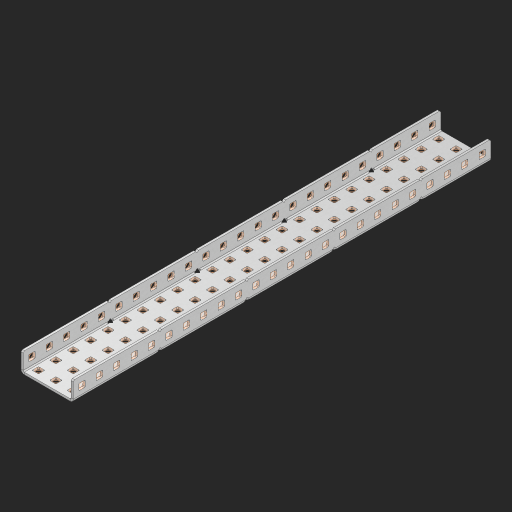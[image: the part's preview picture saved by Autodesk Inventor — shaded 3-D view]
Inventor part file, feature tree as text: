
AUTODESK INVENTOR PART (.ipt)
format: ipt  version: 2023 (Build 270158000, 158)  size: 1,447,936 bytes
history: native  units: in
note: dims shown in document units (in); Inventor stores cm internally (conversion verified against a paired STEP export)
features: other x125, extrude x119, sheet_metal_op x10, sketch x8, mirror x1, pattern_linear x1, chamfer x1
ambient origin geometry x8: Origin, YZ Plane, XZ Plane, XY Plane, X Axis, Y Axis, Z Axis, Center Point
bodies: Solid1 (feature_tree), Body (feature_tree)
feature tree (265):
  other  "Flange Pattern Plane"
  sheet_metal_op  "Flange Pattern"
  sheet_metal_op  "Body Pattern"
  other  "Arc Length"
  mirror  "Notch Mirror"
  pattern_linear  "Notch Pattern"  Spacing1=0.25in  [1 undecoded]
  chamfer  "End Chamfer"
  extrude  "Half Cut"  Depth=0.0625in
  sketch  "Sketch1"  dims[d0=1.5in]
  other  "Plate1"
  sketch  "Sketch2"  dims[d1=12.0in]
  other  "Plate2"
  sheet_metal_op  "Bend1"
  sheet_metal_op  "Corner1"
  sketch  "Sketch3"  dims[d2=0.0625in]
  other  "Flange Pattern Sketch"
  sketch  "Sketch7"  dims[d3=0.0625in]
  other  "Srf1"
  other  "Srf2"
  sketch  "Sketch8"  dims[d4=0.0312in]
  sketch  "Sketch9"  dims[d5=0.125in]
  other  "Srf91"
  sheet_metal_op  "Body Pattern Sketch"
  other  "Srf92"
  sketch  "Sketch13"  dims[d6=0.0625in]
  sketch  "Sketch14"  dims[d7=0.5in d8=90.0deg d9=0.0312in d10=0.25in d11=0.0625in d12=0.0625in d16=0.182in d17=0.02in d18=0.0625in d19=0.0in d20=0.25in d21=0.25in d46=0.172in d47=1.0in d48=0.0in d49=0.182in d50=0.02in d51=0.25in d52=0.25in d53=0.0625in d54=0.0in d55=0.172in d56=1.0in d57=0.0in d60=9.4488in d62=0.5in d63=1.1811in d65=0.5in d85=0.1473in d86=0.1782in d88=0.04in d89=0.0625in d90=0.0in d91=0.04in d92=0.0491in d95=2.5in d96=0.04in d97=0.25in d98=45.0deg d101=0.0in d102=2.497in d131=1.5in d132=9.4488in d134=0.5in d139=0.5in]
  other  "Srf856"
  other  "Srf1310"
  other  "Srf1311"
  other  "Srf1312"
  other  "Srf1376"
  other  "Srf1377"
  other  "Srf1728"
  other  "Srf1755"
  other  "Srf1878"
  other  "Srf1879"
  other  "Srf1880"
  other  "Srf1881"
  other  "Srf1882"
  other  "Srf1883"
  other  "Srf1884"
  other  "Srf1885"
  other  "Srf1886"
  other  "Srf1887"
  other  "Srf1888"
  other  "Srf1889"
  other  "Srf1890"
  other  "Srf1891"
  other  "Srf1892"
  other  "Srf1893"
  other  "Srf1894"
  other  "Srf1895"
  other  "Srf1896"
  other  "Srf1897"
  other  "Srf1898"
  other  "Srf1899"
  other  "Srf1900"
  other  "Srf1901"
  other  "Srf1902"
  other  "Srf1903"
  other  "Srf1904"
  other  "Srf1905"
  other  "Srf1906"
  other  "Srf1907"
  other  "Srf1908"
  other  "Srf1909"
  other  "Srf1910"
  other  "Srf1911"
  other  "Srf1912"
  other  "Srf1913"
  other  "Srf1914"
  other  "Srf1915"
  other  "Srf1916"
  other  "Srf1917"
  other  "Srf1918"
  other  "Srf1919"
  other  "Srf1942"
  other  "Srf1943"
  other  "Srf1944"
  other  "Srf1945"
  other  "Srf1946"
  other  "Srf1947"
  other  "Srf1948"
  other  "Srf1949"
  other  "Srf1950"
  other  "Srf1951"
  other  "Srf1952"
  other  "Srf1953"
  other  "Srf1954"
  other  "Srf1955"
  other  "Srf1956"
  other  "Srf1957"
  other  "Srf1958"
  other  "Srf1959"
  other  "Srf1960"
  other  "Srf1961"
  other  "Srf1962"
  other  "Srf1963"
  other  "Srf1964"
  other  "Srf1965"
  other  "Srf1966"
  other  "Srf1967"
  other  "Srf1968"
  other  "Srf1969"
  other  "Srf1970"
  other  "Srf1971"
  other  "Srf1972"
  other  "Srf1973"
  other  "Srf1974"
  other  "Srf1975"
  other  "Srf1976"
  other  "Srf1977"
  other  "Srf1978"
  other  "Srf1979"
  other  "Srf1980"
  other  "Srf1981"
  other  "Srf1982"
  other  "Srf1983"
  other  "Srf1984"
  other  "Srf1985"
  other  "Srf1986"
  other  "Srf1987"
  other  "Srf1988"
  other  "Srf1989"
  other  "Srf1990"
  other  "Srf1991"
  other  "Srf1992"
  other  "Srf1993"
  other  "Srf1994"
  other  "Srf1995"
  other  "Srf1996"
  other  "Srf1997"
  other  "Srf1998"
  other  "Srf1999"
  other  "Srf2000"
  other  "Srf2001"
  other  "Srf2002"
  other  "Srf2003"
  other  "Srf2004"
  other  "Srf2005"
  other  "Srf2006"
  other  "Srf2007"
  sheet_metal_op  "Flange Stamp"
  sheet_metal_op  "Flange Circle"
  sheet_metal_op  "Body Stamp"
  sheet_metal_op  "Body Circle"
  sheet_metal_op  "Notch"
  extrude  "ExtrusionSrf2"  Depth=0.0625in
  extrude  "ExtrusionSrf92"  Depth=1.5in
  extrude  "ExtrusionSrf856"  Depth=0.02in
  extrude  "ExtrusionSrf1310"  Depth=0.0625in
  extrude  "ExtrusionSrf1311"  TaperAngle=0.0deg  [1 undecoded]
  extrude  "ExtrusionSrf1312"  Depth=0.25in
  extrude  "ExtrusionSrf1376"  Depth=0.25in
  extrude  "ExtrusionSrf1377"  Depth=1.5in
  extrude  "ExtrusionSrf1728"  Depth=1.5in TaperAngle=0.0deg
  extrude  "ExtrusionSrf1755"  Depth=1.5in
  extrude  "ExtrusionSrf1878"  Depth=0.02in
  extrude  "ExtrusionSrf1879"  Depth=0.25in
  extrude  "ExtrusionSrf1880"  Depth=0.25in
  extrude  "ExtrusionSrf1881"  Depth=0.0625in
  extrude  "ExtrusionSrf1882"  TaperAngle=0.0deg  [1 undecoded]
  extrude  "ExtrusionSrf1883"  Depth=1.5in
  extrude  "ExtrusionSrf1884"  Depth=1.5in TaperAngle=0.0deg
  extrude  "ExtrusionSrf1885"  Depth=1.5in
  extrude  "ExtrusionSrf1886"  Depth=1.5in
  extrude  "ExtrusionSrf1887"  Depth=1.5in
  extrude  "ExtrusionSrf1888"  Depth=1.5in
  extrude  "ExtrusionSrf1889"  Depth=1.5in
  extrude  "ExtrusionSrf1890"  Depth=0.0625in
  extrude  "ExtrusionSrf1891"  TaperAngle=0.0deg  [1 undecoded]
  extrude  "ExtrusionSrf1892"  Depth=1.5in
  extrude  "ExtrusionSrf1893"  Depth=1.5in
  extrude  "ExtrusionSrf1894"  Depth=1.5in
  extrude  "ExtrusionSrf1895"  Depth=0.25in TaperAngle=45.0deg
  extrude  "ExtrusionSrf1896"  TaperAngle=0.0deg  [1 undecoded]
  extrude  "ExtrusionSrf1897"  Depth=1.5in
  extrude  "ExtrusionSrf1898"  Depth=1.5in
  extrude  "ExtrusionSrf1899"  Depth=1.5in
  extrude  "ExtrusionSrf1900"  Depth=1.5in
  extrude  "ExtrusionSrf1901"  Depth=1.5in
  extrude  "ExtrusionSrf1902"  [1 undecoded]
  extrude  "ExtrusionSrf1903"  [1 undecoded]
  extrude  "ExtrusionSrf1904"  [1 undecoded]
  extrude  "ExtrusionSrf1905"  [1 undecoded]
  extrude  "ExtrusionSrf1906"  [1 undecoded]
  extrude  "ExtrusionSrf1907"  [1 undecoded]
  extrude  "ExtrusionSrf1908"  [1 undecoded]
  extrude  "ExtrusionSrf1909"  [1 undecoded]
  extrude  "ExtrusionSrf1910"  [1 undecoded]
  extrude  "ExtrusionSrf1911"  [1 undecoded]
  extrude  "ExtrusionSrf1912"  [1 undecoded]
  extrude  "ExtrusionSrf1913"  [1 undecoded]
  extrude  "ExtrusionSrf1914"  [1 undecoded]
  extrude  "ExtrusionSrf1915"  [1 undecoded]
  extrude  "ExtrusionSrf1916"  [1 undecoded]
  extrude  "ExtrusionSrf1917"  [1 undecoded]
  extrude  "ExtrusionSrf1918"  [1 undecoded]
  extrude  "ExtrusionSrf1919"  [1 undecoded]
  extrude  "ExtrusionSrf1942"  [1 undecoded]
  extrude  "ExtrusionSrf1943"  [1 undecoded]
  extrude  "ExtrusionSrf1944"  [1 undecoded]
  extrude  "ExtrusionSrf1945"  [1 undecoded]
  extrude  "ExtrusionSrf1946"  [1 undecoded]
  extrude  "ExtrusionSrf1947"  [1 undecoded]
  extrude  "ExtrusionSrf1948"  [1 undecoded]
  extrude  "ExtrusionSrf1949"  [1 undecoded]
  extrude  "ExtrusionSrf1950"  [1 undecoded]
  extrude  "ExtrusionSrf1951"  [1 undecoded]
  extrude  "ExtrusionSrf1952"  [1 undecoded]
  extrude  "ExtrusionSrf1953"  [1 undecoded]
  extrude  "ExtrusionSrf1954"  [1 undecoded]
  extrude  "ExtrusionSrf1955"  [1 undecoded]
  extrude  "ExtrusionSrf1956"  [1 undecoded]
  extrude  "ExtrusionSrf1957"  [1 undecoded]
  extrude  "ExtrusionSrf1958"  [1 undecoded]
  extrude  "ExtrusionSrf1959"  [1 undecoded]
  extrude  "ExtrusionSrf1960"  [1 undecoded]
  extrude  "ExtrusionSrf1961"  [1 undecoded]
  extrude  "ExtrusionSrf1962"  [1 undecoded]
  extrude  "ExtrusionSrf1963"  [1 undecoded]
  extrude  "ExtrusionSrf1964"  [1 undecoded]
  extrude  "ExtrusionSrf1965"  [1 undecoded]
  extrude  "ExtrusionSrf1966"  [1 undecoded]
  extrude  "ExtrusionSrf1967"  [1 undecoded]
  extrude  "ExtrusionSrf1968"  [1 undecoded]
  extrude  "ExtrusionSrf1969"  [1 undecoded]
  extrude  "ExtrusionSrf1970"  [1 undecoded]
  extrude  "ExtrusionSrf1971"  [1 undecoded]
  extrude  "ExtrusionSrf1972"  [1 undecoded]
  extrude  "ExtrusionSrf1973"  [1 undecoded]
  extrude  "ExtrusionSrf1974"  [1 undecoded]
  extrude  "ExtrusionSrf1975"  [1 undecoded]
  extrude  "ExtrusionSrf1976"  [1 undecoded]
  extrude  "ExtrusionSrf1977"  [1 undecoded]
  extrude  "ExtrusionSrf1978"  [1 undecoded]
  extrude  "ExtrusionSrf1979"  [1 undecoded]
  extrude  "ExtrusionSrf1980"  [1 undecoded]
  extrude  "ExtrusionSrf1981"  [1 undecoded]
  extrude  "ExtrusionSrf1982"  [1 undecoded]
  extrude  "ExtrusionSrf1983"  [1 undecoded]
  extrude  "ExtrusionSrf1984"  [1 undecoded]
  extrude  "ExtrusionSrf1985"  [1 undecoded]
  extrude  "ExtrusionSrf1986"  [1 undecoded]
  extrude  "ExtrusionSrf1987"  [1 undecoded]
  extrude  "ExtrusionSrf1988"  [1 undecoded]
  extrude  "ExtrusionSrf1989"  [1 undecoded]
  extrude  "ExtrusionSrf1990"  [1 undecoded]
  extrude  "ExtrusionSrf1991"  [1 undecoded]
  extrude  "ExtrusionSrf1992"  [1 undecoded]
  extrude  "ExtrusionSrf1993"  [1 undecoded]
  extrude  "ExtrusionSrf1994"  [1 undecoded]
  extrude  "ExtrusionSrf1995"  [1 undecoded]
  extrude  "ExtrusionSrf1996"  [1 undecoded]
  extrude  "ExtrusionSrf1997"  [1 undecoded]
  extrude  "ExtrusionSrf1998"  [1 undecoded]
  extrude  "ExtrusionSrf1999"  [1 undecoded]
  extrude  "ExtrusionSrf2000"  [1 undecoded]
  extrude  "ExtrusionSrf2001"  [1 undecoded]
  extrude  "ExtrusionSrf2002"  [1 undecoded]
  extrude  "ExtrusionSrf2003"  [1 undecoded]
  extrude  "ExtrusionSrf2004"  [1 undecoded]
  extrude  "ExtrusionSrf2005"  [1 undecoded]
  extrude  "ExtrusionSrf2006"  [1 undecoded]
  extrude  "ExtrusionSrf2007"  [1 undecoded]
note: 89 required parameter values undecoded (feature->parameter linkage not recoverable at this tier; creation-order binding heuristic only, values carry confidence <= 0.55)
